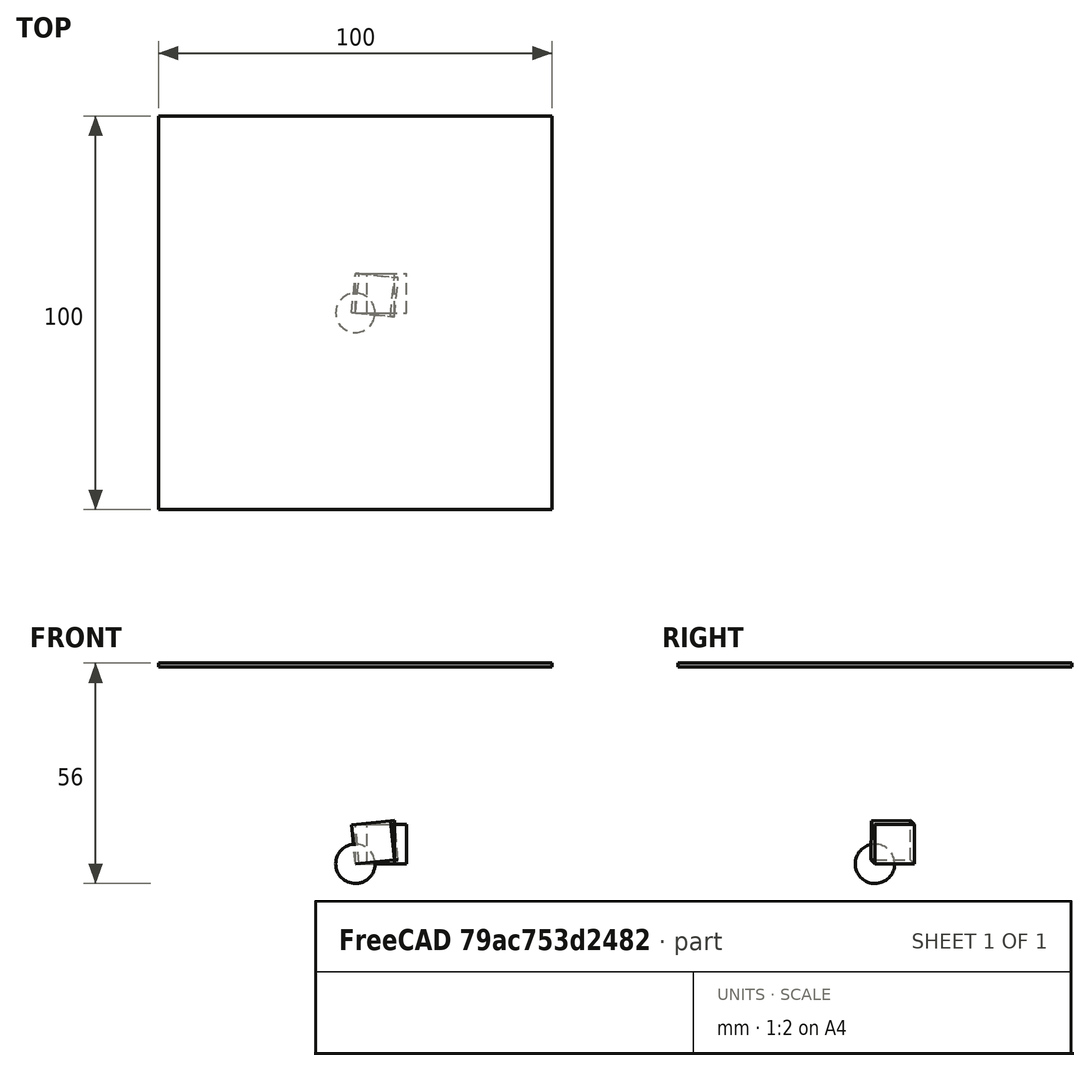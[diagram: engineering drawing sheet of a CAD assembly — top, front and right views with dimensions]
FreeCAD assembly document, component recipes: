
FREECAD ASSEMBLY — COMPONENT RECIPES ("main")

This assembly document has 6 components, labeled P0..P5 below (a component is one placed body or linked part). 0 of them carry a construction recipe — the FreeCAD feature program that regenerates the part from scratch, quoted from this document or its linked companion documents; the rest are supplied as boundary geometry only. No exploded tour is included for this assembly.
COMPONENT P0 — geometry summary ("ShiftedCube001"; no construction recipe available for this part):
  bounding box: 10.0 x 10.0 x 10.0 mm
  tessellated surface: 12 triangles
  volume: 1000 mm^3 (100% of its bounding box)
  symmetry: 4-fold rotationally symmetric about the x axis; 4-fold rotationally symmetric about the y axis; 4-fold rotationally symmetric about the z axis; mirror-symmetric across its x mid-plane, y mid-plane, z mid-plane
COMPONENT P1 — geometry summary ("zlink001"; no construction recipe available for this part):
  bounding box: 10.0 x 10.0 x 10.0 mm
  tessellated surface: 12 triangles
  volume: 1000 mm^3 (100% of its bounding box)
  symmetry: 4-fold rotationally symmetric about the x axis; 4-fold rotationally symmetric about the y axis; 4-fold rotationally symmetric about the z axis; mirror-symmetric across its x mid-plane, y mid-plane, z mid-plane
COMPONENT P2 — geometry summary ("zshift001"; no construction recipe available for this part):
  bounding box: 10.0 x 10.0 x 10.0 mm
  tessellated surface: 12 triangles
  volume: 1000 mm^3 (100% of its bounding box)
  symmetry: 4-fold rotationally symmetric about the x axis; 4-fold rotationally symmetric about the y axis; 4-fold rotationally symmetric about the z axis; mirror-symmetric across its x mid-plane, y mid-plane, z mid-plane
COMPONENT P3 — geometry summary ("Part001"; no construction recipe available for this part):
  bounding box: 11.4 x 10.7 x 10.7 mm
  tessellated surface: 12 triangles
  volume: 1000 mm^3 (76% of its bounding box)
COMPONENT P4 — geometry summary ("Part002"; no construction recipe available for this part):
  bounding box: 28.1 x 17.5 x 13.1 mm
  tessellated surface: 8,012 triangles
  volume: 1524 mm^3 (24% of its bounding box)
COMPONENT P5 — geometry summary ("placementTestsPart"; no construction recipe available for this part):
  bounding box: 43.0 x 13.0 x 13.0 mm
  tessellated surface: 156 triangles
  volume: 13000 mm^3 (179% of its bounding box)
PROVENANCE & LICENSES
A FreeCAD (.FCStd) document from a public repository crawl; recipes are the document's own serialized feature recipes (and, for linked parts, companion documents' recipes).
License: lgpl-3.0.
